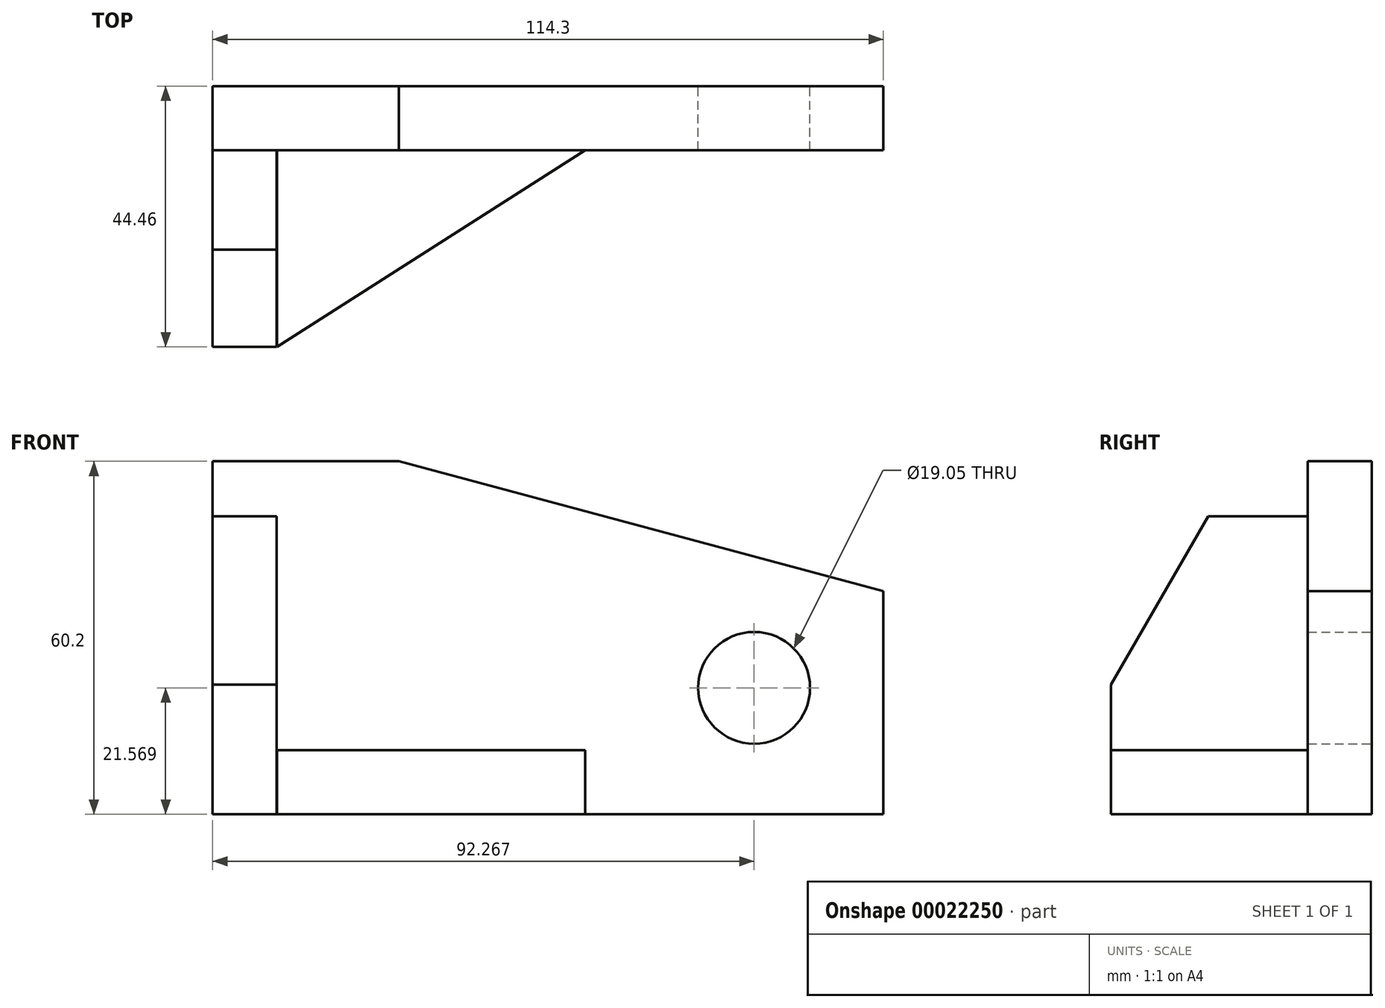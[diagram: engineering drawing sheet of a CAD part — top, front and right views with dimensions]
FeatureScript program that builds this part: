
annotation { "Feature Type Name" : "Feature", "Feature Type Description" : "" }
export const myFeature = defineFeature(function(context is Context, id is Id, definition is map)
    precondition{}
    {
        {
            var Q0;
            Q0=qCreatedBy(makeId("Front.planeOp"),FACE);
            var sketch = newSketch(context, id + "F0", { "sketchPlane" : qUnion([Q0])});
            skLineSegment(sketch, "E0.top", {"start": v(-58, -25.8) * mm, "end": v(56.3, -25.8) * mm});
            skLineSegment(sketch, "E0.left", {"start": v(-58, 34.4) * mm, "end": v(-58, -25.8) * mm});
            skLineSegment(sketch, "E0.right", {"start": v(56.3, 12.27) * mm, "end": v(56.3, -25.8) * mm});
            skLineSegment(sketch, "E1", {"start": v(-26.25, 34.4) * mm, "end": v(56.3, 12.27) * mm});
            skPoint(sketch, "E2.orphan", {"position": v(56.3, 34.4) * mm});
            skLineSegment(sketch, "E3", {"start": v(-58, 34.4) * mm, "end": v(-26.25, 34.4) * mm});
            skCircle(sketch, "E4", {"center": v(34.27, -4.24) * mm, "radius": 9.53 * mm});
            skSolve(sketch);
        }
        {
            var Q0;
            Q0 = qSketchRegion(id + "F0", true);
            extrude(context, id + "F1", {"entities" : qUnion([Q0]), "depth" : 10.92 * mm});
        }
        {
            var Q0;
            Q0=makeQuery(id+"F1.opExtrude","SWEPT_FACE",FACE,{"disambiguationData":[OSD([sQuery(id+"F0.wireOp",EDGE,"E0.left")])]});
            var sketch = newSketch(context, id + "F2", { "sketchPlane" : qUnion([Q0])});
            skLineSegment(sketch, "E5.bottom", {"start": v(10.92, -25.8) * mm, "end": v(44.45, -25.8) * mm});
            skLineSegment(sketch, "E5.top", {"start": v(10.92, 25) * mm, "end": v(27.88, 25) * mm});
            skLineSegment(sketch, "E5.left", {"start": v(10.92, -25.8) * mm, "end": v(10.92, 25) * mm});
            skLineSegment(sketch, "E6", {"start": v(27.88, 25) * mm, "end": v(44.45, -3.7) * mm});
            skPoint(sketch, "E7.orphan", {"position": v(44.45, 25) * mm});
            skLineSegment(sketch, "E8", {"start": v(44.45, -3.7) * mm, "end": v(44.45, -25.8) * mm});
            skSolve(sketch);
        }
        {
            var Q0;
            Q0 = qSketchRegion(id + "F2", true);
            extrude(context, id + "F3", {"entities" : qUnion([Q0]), "oppositeDirection" : true, "depth" : 10.92 * mm});
        }
        {
            var Q0;
            Q0=makeQuery(id+"F1.opExtrude","SWEPT_FACE",FACE,{"disambiguationData":[OSD([sQuery(id+"F0.wireOp",EDGE,"E0.top")])]});
            var sketch = newSketch(context, id + "F4", { "sketchPlane" : qUnion([Q0])});
            skLineSegment(sketch, "E9.bottom", {"start": v(-47.06, 10.92) * mm, "end": v(5.5, 10.92) * mm});
            skLineSegment(sketch, "E9.left", {"start": v(-47.06, 10.92) * mm, "end": v(-47.06, 44.46) * mm});
            skLineSegment(sketch, "E10", {"start": v(-47.06, 44.46) * mm, "end": v(5.5, 10.92) * mm});
            skPoint(sketch, "E9.right.end.orphan", {"position": v(5.5, 44.46) * mm});
            skSolve(sketch);
        }
        {
            var Q0;
            Q0 = qSketchRegion(id + "F4", true);
            extrude(context, id + "F5", {"entities" : qUnion([Q0]), "oppositeDirection" : true, "depth" : 10.92 * mm});
        }
    });
